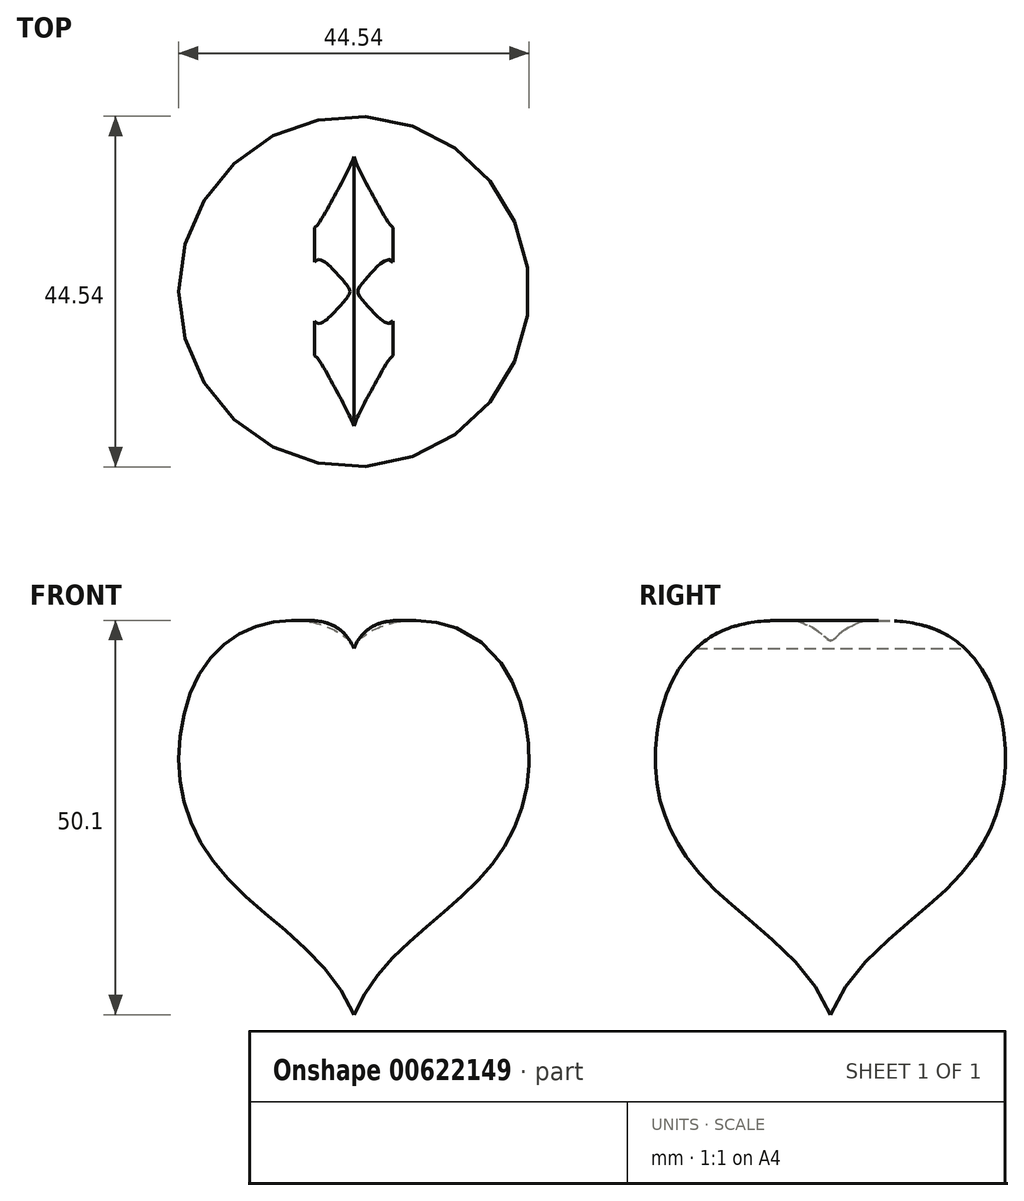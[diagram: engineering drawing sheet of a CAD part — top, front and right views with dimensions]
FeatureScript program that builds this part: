
annotation { "Feature Type Name" : "Feature", "Feature Type Description" : "" }
export const myFeature = defineFeature(function(context is Context, id is Id, definition is map)
    precondition{}
    {
        {
            var Q0;
            Q0=qCreatedBy(makeId("Front.planeOp"),FACE);
            var sketch = newSketch(context, id + "F0", { "sketchPlane" : qUnion([Q0])});
            skLineSegment(sketch, "E0", {"start": v(0, 0) * mm, "end": v(0, -50) * mm});
            skFitSpline(sketch, "E1", {"points": [v(0, -50) * mm, v(-15.41, -33.37) * mm, v(-22.18, -19.5) * mm, v(-18.65, -5.25) * mm, v(-9.54, 0) * mm, v(0, -3) * mm], "startDerivative": vector(-36.9, 88.45) * mm, "endDerivative": vector(44.13, -46.37) * mm});
            skSolve(sketch);
        }
        {
            var Q0;
            Q0 = qSketchRegion(id + "F0", true);
            var Q1;
            Q1=sQuery(id+"F0.wireOp",EDGE,"E0");
            revolve(context, id + "F1", {"entities" : qUnion([Q0]), "axis" : qUnion([Q1]), "revolveType" : RevolveType.FULL});
        }
        {
            var Q0;
            Q0=qCreatedBy(makeId("Front.planeOp"),FACE);
            var sketch = newSketch(context, id + "F2", { "sketchPlane" : qUnion([Q0])});
            skLineSegment(sketch, "E2", {"start": v(0, 0) * mm, "end": v(0, -3.5) * mm, "construction": true});
            skLineSegment(sketch, "E3", {"start": v(-5, 0) * mm, "end": v(5, 0) * mm, "construction": true});
            skArc(sketch, "E4", {"start": v(0, -3.5) * mm, "mid": v(-1.95, -0.96) * mm, "end": v(-5, 0) * mm});
            skArc(sketch, "E5.MirrorCS", {"start": v(0, -3.5) * mm, "mid": v(1.95, -0.96) * mm, "end": v(5, 0) * mm});
            skLineSegment(sketch, "E6", {"start": v(-5, 0) * mm, "end": v(-5, 2.5) * mm});
            skLineSegment(sketch, "E7", {"start": v(-5, 2.5) * mm, "end": v(5, 2.5) * mm});
            skLineSegment(sketch, "E8", {"start": v(5, 2.5) * mm, "end": v(5, 0) * mm});
            skSolve(sketch);
        }
        {
            var Q0;
            Q0 = qSketchRegion(id + "F2", true);
            extrude(context, id + "F3", {"entities" : qUnion([Q0]), "operationType" : NewBodyOperationType.REMOVE, "endBound" : BoundingType.SYMMETRIC, "depth" : 300 * mm, "offsetDistance" : 25 * mm});
        }
    });
